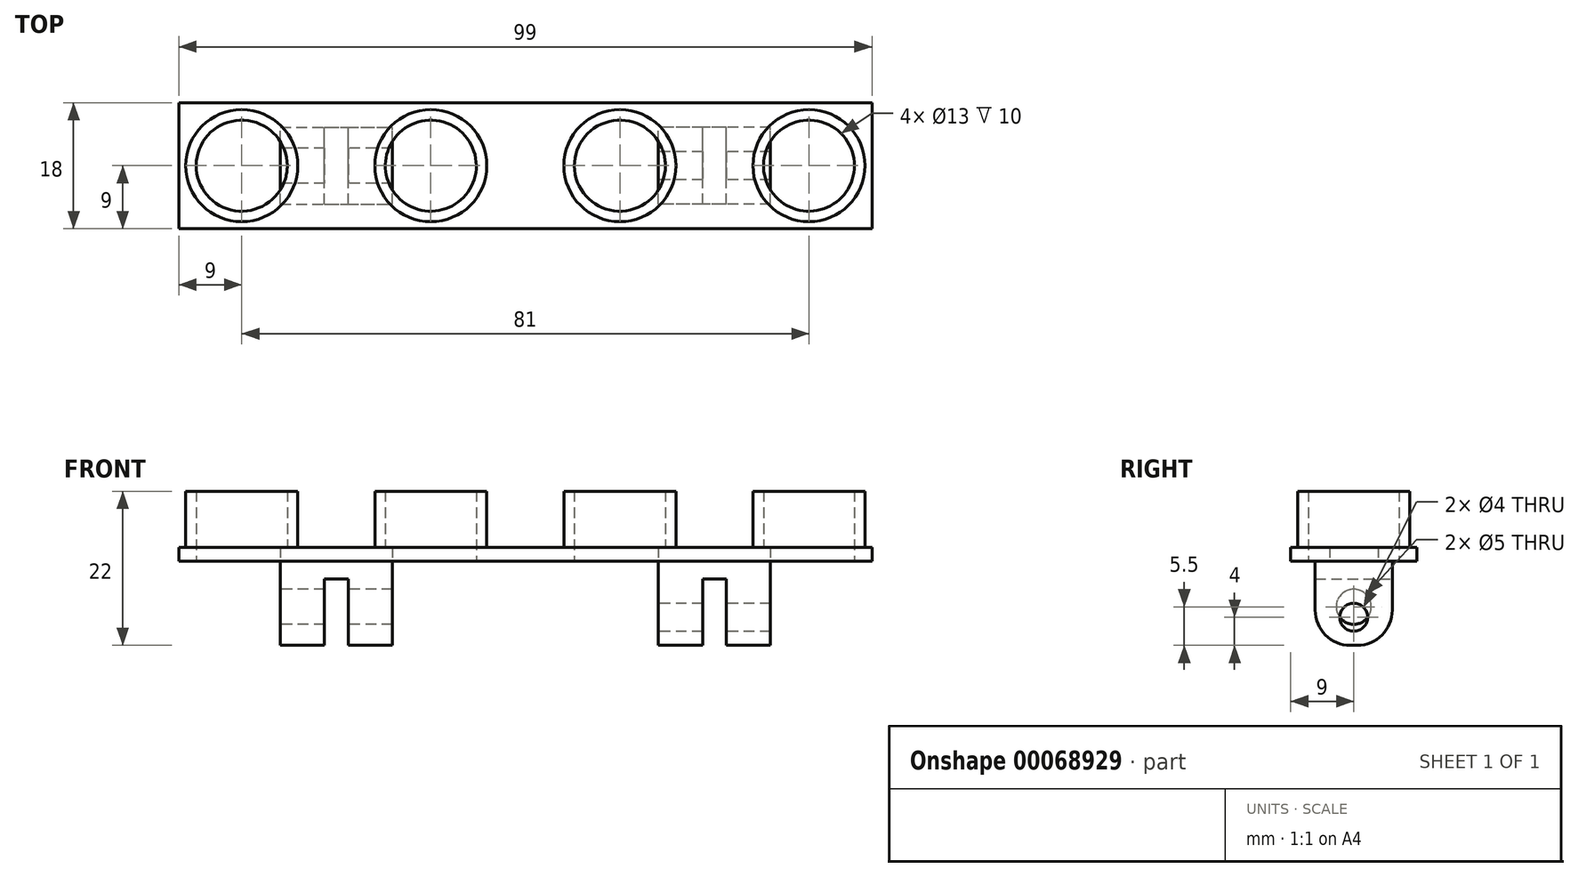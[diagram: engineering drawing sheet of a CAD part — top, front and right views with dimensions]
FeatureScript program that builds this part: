
annotation { "Feature Type Name" : "Feature", "Feature Type Description" : "" }
export const myFeature = defineFeature(function(context is Context, id is Id, definition is map)
    precondition{}
    {
        {
            var Q0;
            Q0=qCreatedBy(makeId("Top.planeOp"),FACE);
            var sketch = newSketch(context, id + "F0", { "sketchPlane" : qUnion([Q0])});
            skLineSegment(sketch, "E0.rect.bottom", {"start": v(-49.5, 9) * mm, "end": v(49.5, 9) * mm});
            skLineSegment(sketch, "E0.rect.top", {"start": v(-49.5, -9) * mm, "end": v(49.5, -9) * mm});
            skLineSegment(sketch, "E0.rect.left", {"start": v(-49.5, 9) * mm, "end": v(-49.5, -9) * mm});
            skLineSegment(sketch, "E0.rect.right", {"start": v(49.5, 9) * mm, "end": v(49.5, -9) * mm});
            skPoint(sketch, "E0.rect.middle", {"position": v(0, 0) * mm});
            skCircle(sketch, "E1", {"center": v(-40.5, 0) * mm, "radius": 8 * mm});
            skCircle(sketch, "E2", {"center": v(-13.5, 0) * mm, "radius": 8 * mm});
            skCircle(sketch, "E3", {"center": v(13.5, 0) * mm, "radius": 8 * mm});
            skCircle(sketch, "E4", {"center": v(40.5, 0) * mm, "radius": 8 * mm});
            skLineSegment(sketch, "E5", {"start": v(-40.5, 0) * mm, "end": v(-13.5, 0) * mm, "construction": true});
            skLineSegment(sketch, "E6", {"start": v(-13.5, 0) * mm, "end": v(13.5, 0) * mm, "construction": true});
            skLineSegment(sketch, "E7", {"start": v(13.5, 0) * mm, "end": v(40.5, 0) * mm, "construction": true});
            skLineSegment(sketch, "E8", {"start": v(-40.5, 0) * mm, "end": v(-49.5, 0) * mm, "construction": true});
            skLineSegment(sketch, "E9", {"start": v(40.5, 0) * mm, "end": v(49.5, 0) * mm, "construction": true});
            skLineSegment(sketch, "E10.bottom", {"start": v(-49.5, -9) * mm, "end": v(0, -9) * mm, "construction": true});
            skLineSegment(sketch, "E10.top", {"start": v(-49.5, 9) * mm, "end": v(0, 9) * mm, "construction": true});
            skLineSegment(sketch, "E10.left", {"start": v(-49.5, -9) * mm, "end": v(-49.5, 9) * mm, "construction": true});
            skLineSegment(sketch, "E10.right", {"start": v(0, -9) * mm, "end": v(0, 9) * mm, "construction": true});
            skLineSegment(sketch, "E11.bottom", {"start": v(0, 9) * mm, "end": v(49.5, 9) * mm, "construction": true});
            skLineSegment(sketch, "E11.top", {"start": v(0, -9) * mm, "end": v(49.5, -9) * mm, "construction": true});
            skLineSegment(sketch, "E11.left", {"start": v(0, 9) * mm, "end": v(0, -9) * mm, "construction": true});
            skLineSegment(sketch, "E11.right", {"start": v(49.5, 9) * mm, "end": v(49.5, -9) * mm, "construction": true});
            skLineSegment(sketch, "E12", {"start": v(-24.75, -9) * mm, "end": v(-24.75, 9) * mm, "construction": true});
            skLineSegment(sketch, "E13", {"start": v(24.75, -9) * mm, "end": v(24.75, 9) * mm, "construction": true});
            skLineSegment(sketch, "E14.rect.top", {"start": v(-27, 9) * mm, "end": v(-23, 9) * mm});
            skPoint(sketch, "E14.rect.middle", {"position": v(-27, 0) * mm});
            skLineSegment(sketch, "E15.MirrorCS", {"start": v(27, 9) * mm, "end": v(23, 9) * mm});
            skPoint(sketch, "E16.MirrorP", {"position": v(27, 0) * mm});
            skLineSegment(sketch, "E17.rect.bottom", {"start": v(-28.7, -5.5) * mm, "end": v(-25.3, -5.5) * mm});
            skLineSegment(sketch, "E17.rect.top", {"start": v(-28.7, 5.5) * mm, "end": v(-25.3, 5.5) * mm});
            skLineSegment(sketch, "E17.rect.left", {"start": v(-28.7, -5.5) * mm, "end": v(-28.7, 5.5) * mm});
            skLineSegment(sketch, "E17.rect.right", {"start": v(-25.3, -5.5) * mm, "end": v(-25.3, 5.5) * mm});
            skLineSegment(sketch, "E18.MirrorCS", {"start": v(25.3, -5.5) * mm, "end": v(25.3, 5.5) * mm});
            skLineSegment(sketch, "E19.MirrorCS", {"start": v(28.7, -5.5) * mm, "end": v(25.3, -5.5) * mm});
            skLineSegment(sketch, "E20.MirrorCS", {"start": v(28.7, 5.5) * mm, "end": v(25.3, 5.5) * mm});
            skLineSegment(sketch, "E21.MirrorCS", {"start": v(28.7, -5.5) * mm, "end": v(28.7, 5.5) * mm});
            skLineSegment(sketch, "E22.MirrorCS", {"start": v(40.5, 0) * mm, "end": v(13.5, 0) * mm, "construction": true});
            skLineSegment(sketch, "E23.bottom", {"start": v(-35, -5.5) * mm, "end": v(-19, -5.5) * mm});
            skLineSegment(sketch, "E23.top", {"start": v(-35, 5.5) * mm, "end": v(-19, 5.5) * mm});
            skLineSegment(sketch, "E23.left", {"start": v(-35, -5.5) * mm, "end": v(-35, 5.5) * mm});
            skLineSegment(sketch, "E23.right", {"start": v(-19, -5.5) * mm, "end": v(-19, 5.5) * mm});
            skLineSegment(sketch, "E24.MirrorCS", {"start": v(19, -5.5) * mm, "end": v(19, 5.5) * mm});
            skLineSegment(sketch, "E25.MirrorCS", {"start": v(35, -5.5) * mm, "end": v(19, -5.5) * mm});
            skLineSegment(sketch, "E26.MirrorCS", {"start": v(35, 5.5) * mm, "end": v(19, 5.5) * mm});
            skLineSegment(sketch, "E27.MirrorCS", {"start": v(35, -5.5) * mm, "end": v(35, 5.5) * mm});
            skSolve(sketch);
        }
        {
            var Q0;
            Q0 = qSketchRegion(id + "F0", true);
            var Q1;
            {var subQ0=sQuery(id+"F0.wireOp",EDGE,"E23.left");var subQ1=sQuery(id+"F0.wireOp",EDGE,"E1");var subQ2=makeQuery(id+"F0.imprint","INTERSECT",VERTEX,{"disambiguationData":[OD(0.0)],"derivedFrom":[subQ1,subQ0]});Q1=makeQuery(id+"F0.imprint","IMPRINT",FACE,{"disambiguationData":[TD([[makeQuery(id+"F0.imprint","IMPRINT",EDGE,{"disambiguationData":[TD([[subQ2,-1.0]])],"derivedFrom":subQ1}),1.0]])]});}
            var Q2;
            {var subQ1=sQuery(id+"F0.wireOp",EDGE,"E17.rect.left");Q2=makeQuery(id+"F0.imprint","IMPRINT",FACE,{"disambiguationData":[TD([[makeQuery(id+"F0.imprint","IMPRINT",EDGE,{"derivedFrom":subQ1}),1.0]])]});}
            var Q3;
            {var subQ0=sQuery(id+"F0.wireOp",EDGE,"E17.rect.left");Q3=makeQuery(id+"F0.imprint","IMPRINT",FACE,{"disambiguationData":[TD([[makeQuery(id+"F0.imprint","IMPRINT",EDGE,{"derivedFrom":subQ0}),-1.0]])]});}
            var Q4;
            {var subQ1=sQuery(id+"F0.wireOp",EDGE,"E17.rect.right");Q4=makeQuery(id+"F0.imprint","IMPRINT",FACE,{"disambiguationData":[TD([[makeQuery(id+"F0.imprint","IMPRINT",EDGE,{"derivedFrom":subQ1}),-1.0]])]});}
            var Q5;
            {var subQ0=sQuery(id+"F0.wireOp",EDGE,"E23.right");var subQ1=sQuery(id+"F0.wireOp",EDGE,"E2");var subQ2=makeQuery(id+"F0.imprint","INTERSECT",VERTEX,{"disambiguationData":[OD(0.0)],"derivedFrom":[subQ1,subQ0]});Q5=makeQuery(id+"F0.imprint","IMPRINT",FACE,{"disambiguationData":[TD([[makeQuery(id+"F0.imprint","IMPRINT",EDGE,{"disambiguationData":[TD([[subQ2,1.0]])],"derivedFrom":subQ1}),1.0]])]});}
            var Q6;
            {var subQ0=sQuery(id+"F0.wireOp",EDGE,"E24.MirrorCS");var subQ1=sQuery(id+"F0.wireOp",EDGE,"E3");var subQ2=makeQuery(id+"F0.imprint","INTERSECT",VERTEX,{"disambiguationData":[OD(0.0)],"derivedFrom":[subQ1,subQ0]});Q6=makeQuery(id+"F0.imprint","IMPRINT",FACE,{"disambiguationData":[TD([[makeQuery(id+"F0.imprint","IMPRINT",EDGE,{"disambiguationData":[TD([[subQ2,-1.0]])],"derivedFrom":subQ1}),1.0]])]});}
            var Q7;
            {var subQ8=sQuery(id+"F0.wireOp",EDGE,"E18.MirrorCS");Q7=makeQuery(id+"F0.imprint","IMPRINT",FACE,{"disambiguationData":[TD([[makeQuery(id+"F0.imprint","IMPRINT",EDGE,{"derivedFrom":subQ8}),1.0]])]});}
            var Q8;
            {var subQ0=sQuery(id+"F0.wireOp",EDGE,"E18.MirrorCS");Q8=makeQuery(id+"F0.imprint","IMPRINT",FACE,{"disambiguationData":[TD([[makeQuery(id+"F0.imprint","IMPRINT",EDGE,{"derivedFrom":subQ0}),-1.0]])]});}
            var Q9;
            {var subQ1=sQuery(id+"F0.wireOp",EDGE,"E21.MirrorCS");Q9=makeQuery(id+"F0.imprint","IMPRINT",FACE,{"disambiguationData":[TD([[makeQuery(id+"F0.imprint","IMPRINT",EDGE,{"derivedFrom":subQ1}),-1.0]])]});}
            var Q10;
            {var subQ0=sQuery(id+"F0.wireOp",EDGE,"E27.MirrorCS");var subQ1=sQuery(id+"F0.wireOp",EDGE,"E4");var subQ2=makeQuery(id+"F0.imprint","INTERSECT",VERTEX,{"disambiguationData":[OD(0.0)],"derivedFrom":[subQ1,subQ0]});Q10=makeQuery(id+"F0.imprint","IMPRINT",FACE,{"disambiguationData":[TD([[makeQuery(id+"F0.imprint","IMPRINT",EDGE,{"disambiguationData":[TD([[subQ2,1.0]])],"derivedFrom":subQ1}),1.0]])]});}
            extrude(context, id + "F1", {"entities" : qUnion([Q0, Q1, Q2, Q3, Q4, Q5, Q6, Q7, Q8, Q9, Q10]), "depth" : 2 * mm});
        }
        {
            var Q0;
            {var subQ0=sQuery(id+"F0.wireOp",EDGE,"E23.left");var subQ1=sQuery(id+"F0.wireOp",EDGE,"E1");var subQ2=makeQuery(id+"F0.imprint","INTERSECT",VERTEX,{"disambiguationData":[OD(0.0)],"derivedFrom":[subQ1,subQ0]});Q0=makeQuery(id+"F0.imprint","IMPRINT",FACE,{"disambiguationData":[TD([[makeQuery(id+"F0.imprint","IMPRINT",EDGE,{"disambiguationData":[TD([[subQ2,1.0]])],"derivedFrom":subQ1}),1.0]])]});}
            var Q1;
            {var subQ0=sQuery(id+"F0.wireOp",EDGE,"E23.right");var subQ1=sQuery(id+"F0.wireOp",EDGE,"E2");var subQ2=makeQuery(id+"F0.imprint","INTERSECT",VERTEX,{"disambiguationData":[OD(0.0)],"derivedFrom":[subQ1,subQ0]});Q1=makeQuery(id+"F0.imprint","IMPRINT",FACE,{"disambiguationData":[TD([[makeQuery(id+"F0.imprint","IMPRINT",EDGE,{"disambiguationData":[TD([[subQ2,-1.0]])],"derivedFrom":subQ1}),1.0]])]});}
            var Q2;
            {var subQ0=sQuery(id+"F0.wireOp",EDGE,"E24.MirrorCS");var subQ1=sQuery(id+"F0.wireOp",EDGE,"E3");var subQ2=makeQuery(id+"F0.imprint","INTERSECT",VERTEX,{"disambiguationData":[OD(0.0)],"derivedFrom":[subQ1,subQ0]});Q2=makeQuery(id+"F0.imprint","IMPRINT",FACE,{"disambiguationData":[TD([[makeQuery(id+"F0.imprint","IMPRINT",EDGE,{"disambiguationData":[TD([[subQ2,1.0]])],"derivedFrom":subQ1}),1.0]])]});}
            var Q3;
            {var subQ0=sQuery(id+"F0.wireOp",EDGE,"E27.MirrorCS");var subQ1=sQuery(id+"F0.wireOp",EDGE,"E4");var subQ2=makeQuery(id+"F0.imprint","INTERSECT",VERTEX,{"disambiguationData":[OD(0.0)],"derivedFrom":[subQ1,subQ0]});Q3=makeQuery(id+"F0.imprint","IMPRINT",FACE,{"disambiguationData":[TD([[makeQuery(id+"F0.imprint","IMPRINT",EDGE,{"disambiguationData":[TD([[subQ2,-1.0]])],"derivedFrom":subQ1}),1.0]])]});}
            var Q4;
            {var subQ0=sQuery(id+"F0.wireOp",EDGE,"E23.left");var subQ1=sQuery(id+"F0.wireOp",EDGE,"E1");var subQ2=makeQuery(id+"F0.imprint","INTERSECT",VERTEX,{"disambiguationData":[OD(0.0)],"derivedFrom":[subQ1,subQ0]});Q4=makeQuery(id+"F0.imprint","IMPRINT",FACE,{"disambiguationData":[TD([[makeQuery(id+"F0.imprint","IMPRINT",EDGE,{"disambiguationData":[TD([[subQ2,-1.0]])],"derivedFrom":subQ1}),1.0]])]});}
            var Q5;
            {var subQ0=sQuery(id+"F0.wireOp",EDGE,"E23.right");var subQ1=sQuery(id+"F0.wireOp",EDGE,"E2");var subQ2=makeQuery(id+"F0.imprint","INTERSECT",VERTEX,{"disambiguationData":[OD(0.0)],"derivedFrom":[subQ1,subQ0]});Q5=makeQuery(id+"F0.imprint","IMPRINT",FACE,{"disambiguationData":[TD([[makeQuery(id+"F0.imprint","IMPRINT",EDGE,{"disambiguationData":[TD([[subQ2,1.0]])],"derivedFrom":subQ1}),1.0]])]});}
            var Q6;
            {var subQ0=sQuery(id+"F0.wireOp",EDGE,"E24.MirrorCS");var subQ1=sQuery(id+"F0.wireOp",EDGE,"E3");var subQ2=makeQuery(id+"F0.imprint","INTERSECT",VERTEX,{"disambiguationData":[OD(0.0)],"derivedFrom":[subQ1,subQ0]});Q6=makeQuery(id+"F0.imprint","IMPRINT",FACE,{"disambiguationData":[TD([[makeQuery(id+"F0.imprint","IMPRINT",EDGE,{"disambiguationData":[TD([[subQ2,-1.0]])],"derivedFrom":subQ1}),1.0]])]});}
            var Q7;
            {var subQ0=sQuery(id+"F0.wireOp",EDGE,"E27.MirrorCS");var subQ1=sQuery(id+"F0.wireOp",EDGE,"E4");var subQ2=makeQuery(id+"F0.imprint","INTERSECT",VERTEX,{"disambiguationData":[OD(0.0)],"derivedFrom":[subQ1,subQ0]});Q7=makeQuery(id+"F0.imprint","IMPRINT",FACE,{"disambiguationData":[TD([[makeQuery(id+"F0.imprint","IMPRINT",EDGE,{"disambiguationData":[TD([[subQ2,1.0]])],"derivedFrom":subQ1}),1.0]])]});}
            extrude(context, id + "F2", {"entities" : qUnion([Q0, Q1, Q2, Q3, Q4, Q5, Q6, Q7]), "operationType" : NewBodyOperationType.ADD, "depth" : 10 * mm});
        }
        {
            var Q0;
            Q0=makeQuery(id+"F2.opExtrude","CAP_FACE",FACE,{"disambiguationData":[OSD([sQuery(id+"F0.wireOp",EDGE,"E1")])],"isStart":false});
            var Q1;
            Q1=makeQuery(id+"F2.opExtrude","CAP_FACE",FACE,{"disambiguationData":[OSD([sQuery(id+"F0.wireOp",EDGE,"E2")])],"isStart":false});
            var Q2;
            Q2=makeQuery(id+"F2.opExtrude","CAP_FACE",FACE,{"disambiguationData":[OSD([sQuery(id+"F0.wireOp",EDGE,"E3")])],"isStart":false});
            var Q3;
            Q3=makeQuery(id+"F2.opExtrude","CAP_FACE",FACE,{"disambiguationData":[OSD([sQuery(id+"F0.wireOp",EDGE,"E4")])],"isStart":false});
            shell(context, id + "F3", {"entities" : qUnion([Q0, Q1, Q2, Q3]), "thickness" : 1.5 * mm});
        }
        {
            var Q0;
            Q0=makeQuery(id+"F3.opShell","OFFSET_FACE",FACE,{"disambiguationData":[OSD([sQuery(id+"F0.wireOp",EDGE,"E0.rect.bottom"),sQuery(id+"F0.wireOp",EDGE,"E0.rect.top"),sQuery(id+"F0.wireOp",EDGE,"E0.rect.left"),sQuery(id+"F0.wireOp",EDGE,"E0.rect.right"),sQuery(id+"F0.wireOp",EDGE,"E1"),sQuery(id+"F0.wireOp",EDGE,"E2"),sQuery(id+"F0.wireOp",EDGE,"E3"),sQuery(id+"F0.wireOp",EDGE,"E4")]),OD(0.0)]});
            var Q1;
            Q1=makeQuery(id+"F3.opShell","OFFSET_FACE",FACE,{"disambiguationData":[OSD([sQuery(id+"F0.wireOp",EDGE,"E0.rect.bottom"),sQuery(id+"F0.wireOp",EDGE,"E0.rect.top"),sQuery(id+"F0.wireOp",EDGE,"E0.rect.left"),sQuery(id+"F0.wireOp",EDGE,"E0.rect.right"),sQuery(id+"F0.wireOp",EDGE,"E1"),sQuery(id+"F0.wireOp",EDGE,"E2"),sQuery(id+"F0.wireOp",EDGE,"E3"),sQuery(id+"F0.wireOp",EDGE,"E4")]),OD(1.0)]});
            var Q2;
            Q2=makeQuery(id+"F3.opShell","OFFSET_FACE",FACE,{"disambiguationData":[OSD([sQuery(id+"F0.wireOp",EDGE,"E0.rect.bottom"),sQuery(id+"F0.wireOp",EDGE,"E0.rect.top"),sQuery(id+"F0.wireOp",EDGE,"E0.rect.left"),sQuery(id+"F0.wireOp",EDGE,"E0.rect.right"),sQuery(id+"F0.wireOp",EDGE,"E1"),sQuery(id+"F0.wireOp",EDGE,"E2"),sQuery(id+"F0.wireOp",EDGE,"E3"),sQuery(id+"F0.wireOp",EDGE,"E4")]),OD(2.0)]});
            var Q3;
            Q3=makeQuery(id+"F3.opShell","OFFSET_FACE",FACE,{"disambiguationData":[OSD([sQuery(id+"F0.wireOp",EDGE,"E0.rect.bottom"),sQuery(id+"F0.wireOp",EDGE,"E0.rect.top"),sQuery(id+"F0.wireOp",EDGE,"E0.rect.left"),sQuery(id+"F0.wireOp",EDGE,"E0.rect.right"),sQuery(id+"F0.wireOp",EDGE,"E1"),sQuery(id+"F0.wireOp",EDGE,"E2"),sQuery(id+"F0.wireOp",EDGE,"E3"),sQuery(id+"F0.wireOp",EDGE,"E4")]),OD(3.0)]});
            extrude(context, id + "F4", {"entities" : qUnion([Q0, Q1, Q2, Q3]), "operationType" : NewBodyOperationType.REMOVE, "oppositeDirection" : true, "depth" : 5 * mm});
        }
        {
            var Q0;
            {var subQ5=sQuery(id+"F0.wireOp",EDGE,"E27.MirrorCS");Q0=makeQuery(id+"F0.imprint","IMPRINT",FACE,{"disambiguationData":[TD([[makeQuery(id+"F0.imprint","IMPRINT",EDGE,{"derivedFrom":subQ5}),1.0]])]});}
            var Q1;
            {var subQ5=sQuery(id+"F0.wireOp",EDGE,"E17.rect.left");Q1=makeQuery(id+"F0.imprint","IMPRINT",FACE,{"disambiguationData":[TD([[makeQuery(id+"F0.imprint","IMPRINT",EDGE,{"derivedFrom":subQ5}),1.0]])]});}
            var Q2;
            {var subQ5=sQuery(id+"F0.wireOp",EDGE,"E17.rect.right");Q2=makeQuery(id+"F0.imprint","IMPRINT",FACE,{"disambiguationData":[TD([[makeQuery(id+"F0.imprint","IMPRINT",EDGE,{"derivedFrom":subQ5}),-1.0]])]});}
            var Q3;
            {var subQ5=sQuery(id+"F0.wireOp",EDGE,"E18.MirrorCS");Q3=makeQuery(id+"F0.imprint","IMPRINT",FACE,{"disambiguationData":[TD([[makeQuery(id+"F0.imprint","IMPRINT",EDGE,{"derivedFrom":subQ5}),1.0]])]});}
            var Q4;
            {var subQ5=sQuery(id+"F0.wireOp",EDGE,"E21.MirrorCS");Q4=makeQuery(id+"F0.imprint","IMPRINT",FACE,{"disambiguationData":[TD([[makeQuery(id+"F0.imprint","IMPRINT",EDGE,{"derivedFrom":subQ5}),-1.0]])]});}
            var Q5;
            {var subQ5=sQuery(id+"F0.wireOp",EDGE,"E23.left");Q5=makeQuery(id+"F0.imprint","IMPRINT",FACE,{"disambiguationData":[TD([[makeQuery(id+"F0.imprint","IMPRINT",EDGE,{"derivedFrom":subQ5}),-1.0]])]});}
            var Q6;
            {var subQ5=sQuery(id+"F0.wireOp",EDGE,"E23.right");Q6=makeQuery(id+"F0.imprint","IMPRINT",FACE,{"disambiguationData":[TD([[makeQuery(id+"F0.imprint","IMPRINT",EDGE,{"derivedFrom":subQ5}),1.0]])]});}
            var Q7;
            {var subQ5=sQuery(id+"F0.wireOp",EDGE,"E24.MirrorCS");Q7=makeQuery(id+"F0.imprint","IMPRINT",FACE,{"disambiguationData":[TD([[makeQuery(id+"F0.imprint","IMPRINT",EDGE,{"derivedFrom":subQ5}),-1.0]])]});}
            extrude(context, id + "F5", {"entities" : qUnion([Q0, Q1, Q2, Q3, Q4, Q5, Q6, Q7]), "operationType" : NewBodyOperationType.ADD, "oppositeDirection" : true, "depth" : 12 * mm, "hasSecondDirection" : true, "secondDirectionOppositeDirection" : false, "secondDirectionDepth" : 2 * mm});
        }
        {
            var Q0;
            Q0=makeQuery(id+"F5.opExtrude","SWEPT_FACE",FACE,{"disambiguationData":[OSD([sQuery(id+"F0.wireOp",EDGE,"E17.rect.left")])]});
            var sketch = newSketch(context, id + "F6", { "sketchPlane" : qUnion([Q0])});
            skCircle(sketch, "E28", {"center": v(0, -6.5) * mm, "radius": 5.5 * mm});
            skCircle(sketch, "E29", {"center": v(0, -6.5) * mm, "radius": 2.5 * mm});
            skSolve(sketch);
        }
        {
            var Q0;
            Q0=makeQuery(id+"F5.opExtrude","SWEPT_FACE",FACE,{"disambiguationData":[OSD([sQuery(id+"F0.wireOp",EDGE,"E18.MirrorCS")])]});
            var sketch = newSketch(context, id + "F7", { "sketchPlane" : qUnion([Q0])});
            skCircle(sketch, "E30", {"center": v(0, -8) * mm, "radius": 4 * mm});
            skCircle(sketch, "E31", {"center": v(0, -8) * mm, "radius": 2 * mm});
            skSolve(sketch);
        }
        {
            var Q0;
            {var subQ0=sQuery(id+"F0.wireOp",EDGE,"E23.bottom");Q0=makeQuery(id+"F5.opExtrude","CAP_EDGE",EDGE,{"disambiguationData":[OSD([subQ0]),TDD([makeQuery(id+"F0.imprint","IMPRINT",EDGE,{"disambiguationData":[TD([[makeQuery(id+"F0.imprint","INTERSECT",VERTEX,{"derivedFrom":[sQuery(id+"F0.wireOp",EDGE,"E17.rect.left"),subQ0]}),1.0]])],"derivedFrom":subQ0})])],"isStart":false});}
            var Q1;
            {var subQ0=sQuery(id+"F0.wireOp",EDGE,"E23.bottom");Q1=makeQuery(id+"F5.opExtrude","CAP_EDGE",EDGE,{"disambiguationData":[OSD([subQ0]),TDD([makeQuery(id+"F0.imprint","IMPRINT",EDGE,{"disambiguationData":[TD([[makeQuery(id+"F0.imprint","INTERSECT",VERTEX,{"derivedFrom":[sQuery(id+"F0.wireOp",EDGE,"E17.rect.right"),subQ0]}),-1.0]])],"derivedFrom":subQ0})])],"isStart":false});}
            var Q2;
            {var subQ0=sQuery(id+"F0.wireOp",EDGE,"E25.MirrorCS");Q2=makeQuery(id+"F5.opExtrude","CAP_EDGE",EDGE,{"disambiguationData":[OSD([subQ0]),TDD([makeQuery(id+"F0.imprint","IMPRINT",EDGE,{"disambiguationData":[TD([[makeQuery(id+"F0.imprint","INTERSECT",VERTEX,{"derivedFrom":[sQuery(id+"F0.wireOp",EDGE,"E18.MirrorCS"),subQ0]}),-1.0]])],"derivedFrom":subQ0})])],"isStart":false});}
            var Q3;
            {var subQ0=sQuery(id+"F0.wireOp",EDGE,"E25.MirrorCS");Q3=makeQuery(id+"F5.opExtrude","CAP_EDGE",EDGE,{"disambiguationData":[OSD([subQ0]),TDD([makeQuery(id+"F0.imprint","IMPRINT",EDGE,{"disambiguationData":[TD([[makeQuery(id+"F0.imprint","INTERSECT",VERTEX,{"derivedFrom":[sQuery(id+"F0.wireOp",EDGE,"E21.MirrorCS"),subQ0]}),1.0]])],"derivedFrom":subQ0})])],"isStart":false});}
            var Q4;
            {var subQ0=sQuery(id+"F0.wireOp",EDGE,"E23.top");Q4=makeQuery(id+"F5.opExtrude","CAP_EDGE",EDGE,{"disambiguationData":[OSD([subQ0]),TDD([makeQuery(id+"F0.imprint","IMPRINT",EDGE,{"disambiguationData":[TD([[makeQuery(id+"F0.imprint","INTERSECT",VERTEX,{"derivedFrom":[sQuery(id+"F0.wireOp",EDGE,"E17.rect.left"),subQ0]}),1.0]])],"derivedFrom":subQ0})])],"isStart":false});}
            var Q5;
            {var subQ0=sQuery(id+"F0.wireOp",EDGE,"E23.top");Q5=makeQuery(id+"F5.opExtrude","CAP_EDGE",EDGE,{"disambiguationData":[OSD([subQ0]),TDD([makeQuery(id+"F0.imprint","IMPRINT",EDGE,{"disambiguationData":[TD([[makeQuery(id+"F0.imprint","INTERSECT",VERTEX,{"derivedFrom":[sQuery(id+"F0.wireOp",EDGE,"E17.rect.right"),subQ0]}),-1.0]])],"derivedFrom":subQ0})])],"isStart":false});}
            var Q6;
            {var subQ0=sQuery(id+"F0.wireOp",EDGE,"E26.MirrorCS");Q6=makeQuery(id+"F5.opExtrude","CAP_EDGE",EDGE,{"disambiguationData":[OSD([subQ0]),TDD([makeQuery(id+"F0.imprint","IMPRINT",EDGE,{"disambiguationData":[TD([[makeQuery(id+"F0.imprint","INTERSECT",VERTEX,{"derivedFrom":[sQuery(id+"F0.wireOp",EDGE,"E18.MirrorCS"),subQ0]}),-1.0]])],"derivedFrom":subQ0})])],"isStart":false});}
            var Q7;
            {var subQ0=sQuery(id+"F0.wireOp",EDGE,"E26.MirrorCS");Q7=makeQuery(id+"F5.opExtrude","CAP_EDGE",EDGE,{"disambiguationData":[OSD([subQ0]),TDD([makeQuery(id+"F0.imprint","IMPRINT",EDGE,{"disambiguationData":[TD([[makeQuery(id+"F0.imprint","INTERSECT",VERTEX,{"derivedFrom":[sQuery(id+"F0.wireOp",EDGE,"E21.MirrorCS"),subQ0]}),1.0]])],"derivedFrom":subQ0})])],"isStart":false});}
            fillet(context, id + "F8", {"entities" : qUnion([Q0, Q1, Q2, Q3, Q4, Q5, Q6, Q7]), "radius" : 5 * mm, "tangentPropagation" : true, "allowEdgeOverflow" : false});
        }
        {
            var Q0;
            Q0=makeQuery(id+"F7.imprint","IMPRINT",FACE,{"disambiguationData":[TD([[makeQuery(id+"F7.imprint","IMPRINT",EDGE,{"derivedFrom":sQuery(id+"F7.wireOp",EDGE,"E31")}),1.0]])]});
            var Q1;
            Q1=makeQuery(id+"F6.imprint","IMPRINT",FACE,{"disambiguationData":[TD([[makeQuery(id+"F6.imprint","IMPRINT",EDGE,{"derivedFrom":sQuery(id+"F6.wireOp",EDGE,"E29")}),1.0]])]});
            extrude(context, id + "F9", {"entities" : qUnion([Q0, Q1]), "operationType" : NewBodyOperationType.REMOVE, "depth" : 10 * mm, "hasSecondDirection" : true, "secondDirectionOppositeDirection" : true, "secondDirectionDepth" : 10 * mm});
        }
        {
            var Q0;
            {var subQ0=sQuery(id+"F0.wireOp",EDGE,"E17.rect.left");Q0=makeQuery(id+"F0.imprint","IMPRINT",FACE,{"disambiguationData":[TD([[makeQuery(id+"F0.imprint","IMPRINT",EDGE,{"derivedFrom":subQ0}),-1.0]])]});}
            var Q1;
            {var subQ0=sQuery(id+"F0.wireOp",EDGE,"E18.MirrorCS");Q1=makeQuery(id+"F0.imprint","IMPRINT",FACE,{"disambiguationData":[TD([[makeQuery(id+"F0.imprint","IMPRINT",EDGE,{"derivedFrom":subQ0}),-1.0]])]});}
            extrude(context, id + "F10", {"entities" : qUnion([Q0, Q1]), "operationType" : NewBodyOperationType.ADD, "oppositeDirection" : true, "depth" : 2.5 * mm, "hasSecondDirection" : true, "secondDirectionOppositeDirection" : false, "secondDirectionDepth" : 2 * mm});
        }
    });
